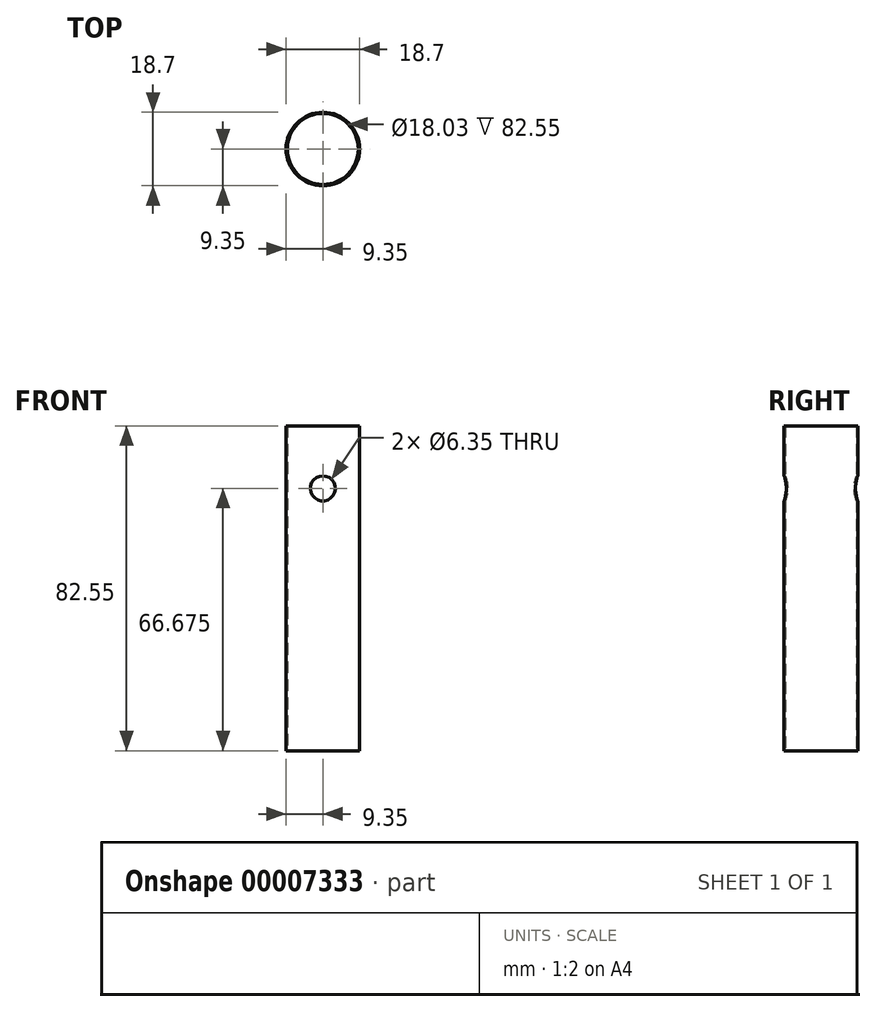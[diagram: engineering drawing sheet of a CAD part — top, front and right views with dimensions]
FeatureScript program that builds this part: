
annotation { "Feature Type Name" : "Feature", "Feature Type Description" : "" }
export const myFeature = defineFeature(function(context is Context, id is Id, definition is map)
    precondition{}
    {
        {
            var Q0;
            Q0=qCreatedBy(makeId("Front.planeOp"),FACE);
            var sketch = newSketch(context, id + "F0", { "sketchPlane" : qUnion([Q0])});
            skLineSegment(sketch, "E0.bottom", {"start": v(9.02, 0) * mm, "end": v(9.35, 0) * mm});
            skLineSegment(sketch, "E0.top", {"start": v(9.02, 82.55) * mm, "end": v(9.35, 82.55) * mm});
            skLineSegment(sketch, "E0.left", {"start": v(9.02, 0) * mm, "end": v(9.02, 82.55) * mm});
            skLineSegment(sketch, "E0.right", {"start": v(9.35, 0) * mm, "end": v(9.35, 82.55) * mm});
            skLineSegment(sketch, "E1", {"start": v(9.02, 0) * mm, "end": v(0, 0) * mm});
            skLineSegment(sketch, "E2", {"start": v(0, 0) * mm, "end": v(0, 82.55) * mm});
            skSolve(sketch);
        }
        {
            var Q0;
            Q0 = qSketchRegion(id + "F0", true);
            var Q1;
            Q1=sQuery(id+"F0.wireOp",EDGE,"E2");
            revolve(context, id + "F1", {"entities" : qUnion([Q0]), "axis" : qUnion([Q1]), "revolveType" : RevolveType.FULL});
        }
        {
            var Q0;
            Q0=qCreatedBy(makeId("Front.planeOp"),FACE);
            var sketch = newSketch(context, id + "F2", { "sketchPlane" : qUnion([Q0])});
            skLineSegment(sketch, "E3", {"start": v(0, 0) * mm, "end": v(0, 82.55) * mm});
            skCircle(sketch, "E4", {"center": v(0, 66.67) * mm, "radius": 3.18 * mm});
            skSolve(sketch);
        }
        {
            var Q0;
            Q0 = qSketchRegion(id + "F2", true);
            extrude(context, id + "F3", {"entities" : qUnion([Q0]), "operationType" : NewBodyOperationType.REMOVE, "endBound" : BoundingType.THROUGH_ALL, "oppositeDirection" : true, "depth" : 25.4 * mm});
        }
        {
            var Q0;
            Q0 = qSketchRegion(id + "F2", true);
            extrude(context, id + "F4", {"entities" : qUnion([Q0]), "operationType" : NewBodyOperationType.REMOVE, "endBound" : BoundingType.THROUGH_ALL, "depth" : 25.4 * mm});
        }
        {
            var Q0;
            Q0=qCreatedBy(makeId("Top.planeOp"),FACE);
            var sketch = newSketch(context, id + "F5", { "sketchPlane" : qUnion([Q0])});
            skCircle(sketch, "E5.0", {"center": v(0, 0) * mm, "radius": 9.35 * mm});
            skCircle(sketch, "E6", {"center": v(0, 0) * mm, "radius": 63.5 * mm});
            skLineSegment(sketch, "E7", {"start": v(0, 0) * mm, "end": v(0, 63.5) * mm});
            skLineSegment(sketch, "E8", {"start": v(0, 0) * mm, "end": v(55, -31.75) * mm});
            skLineSegment(sketch, "E9", {"start": v(0, 0) * mm, "end": v(-55, -31.75) * mm});
            skPoint(sketch, "E10", {"position": v(0, 9.35) * mm});
            skPoint(sketch, "E11", {"position": v(8.1, -4.67) * mm});
            skPoint(sketch, "E12", {"position": v(-8.1, -4.67) * mm});
            skSolve(sketch);
        }
        {
            var Q0;
            Q0=qCreatedBy(makeId("Top.planeOp"),FACE);
            var sketch = newSketch(context, id + "F6", { "sketchPlane" : qUnion([Q0])});
            skCircle(sketch, "E13.0", {"center": v(0, 0) * mm, "radius": 63.5 * mm});
            skCircle(sketch, "E14.0", {"center": v(0, 0) * mm, "radius": 9.35 * mm});
            skLineSegment(sketch, "E15.0", {"start": v(0, 0) * mm, "end": v(0, 63.5) * mm});
            skLineSegment(sketch, "E16", {"start": v(0, 0) * mm, "end": v(63.5, 0) * mm});
            skLineSegment(sketch, "E17", {"start": v(0, 0) * mm, "end": v(0, -63.5) * mm});
            skLineSegment(sketch, "E18", {"start": v(0, 0) * mm, "end": v(-63.5, 0) * mm});
            skPoint(sketch, "E19", {"position": v(0, 9.35) * mm});
            skPoint(sketch, "E20", {"position": v(9.35, 0) * mm});
            skPoint(sketch, "E21", {"position": v(0, -9.35) * mm});
            skPoint(sketch, "E22", {"position": v(-9.35, 0) * mm});
            skLineSegment(sketch, "E23", {"start": v(0, 0) * mm, "end": v(44.9, 44.9) * mm});
            skPoint(sketch, "E24", {"position": v(6.6, 6.6) * mm});
            skSolve(sketch);
        }
        {
            var Q0;
            Q0=qCreatedBy(makeId("Top.planeOp"),FACE);
            var sketch = newSketch(context, id + "F7", { "sketchPlane" : qUnion([Q0])});
            skCircle(sketch, "E25.0", {"center": v(0, 0) * mm, "radius": 63.5 * mm});
            skLineSegment(sketch, "E26.0", {"start": v(0, 0) * mm, "end": v(0, 63.5) * mm});
            skCircle(sketch, "E27.0", {"center": v(0, 0) * mm, "radius": 9.35 * mm});
            skLineSegment(sketch, "E28", {"start": v(0, 0) * mm, "end": v(60.4, 19.62) * mm});
            skLineSegment(sketch, "E29", {"start": v(0, 0) * mm, "end": v(37.32, -51.37) * mm});
            skLineSegment(sketch, "E30.0.MirrorCS", {"start": v(0, 0) * mm, "end": v(-60.4, 19.62) * mm});
            skLineSegment(sketch, "E31.0.MirrorCS", {"start": v(0, 0) * mm, "end": v(-37.32, -51.37) * mm});
            skPoint(sketch, "E32", {"position": v(0, 9.35) * mm});
            skPoint(sketch, "E33", {"position": v(8.89, 2.89) * mm});
            skPoint(sketch, "E34", {"position": v(-8.89, 2.89) * mm});
            skPoint(sketch, "E35", {"position": v(-5.5, -7.56) * mm});
            skPoint(sketch, "E36", {"position": v(5.5, -7.56) * mm});
            skSolve(sketch);
        }
    });
